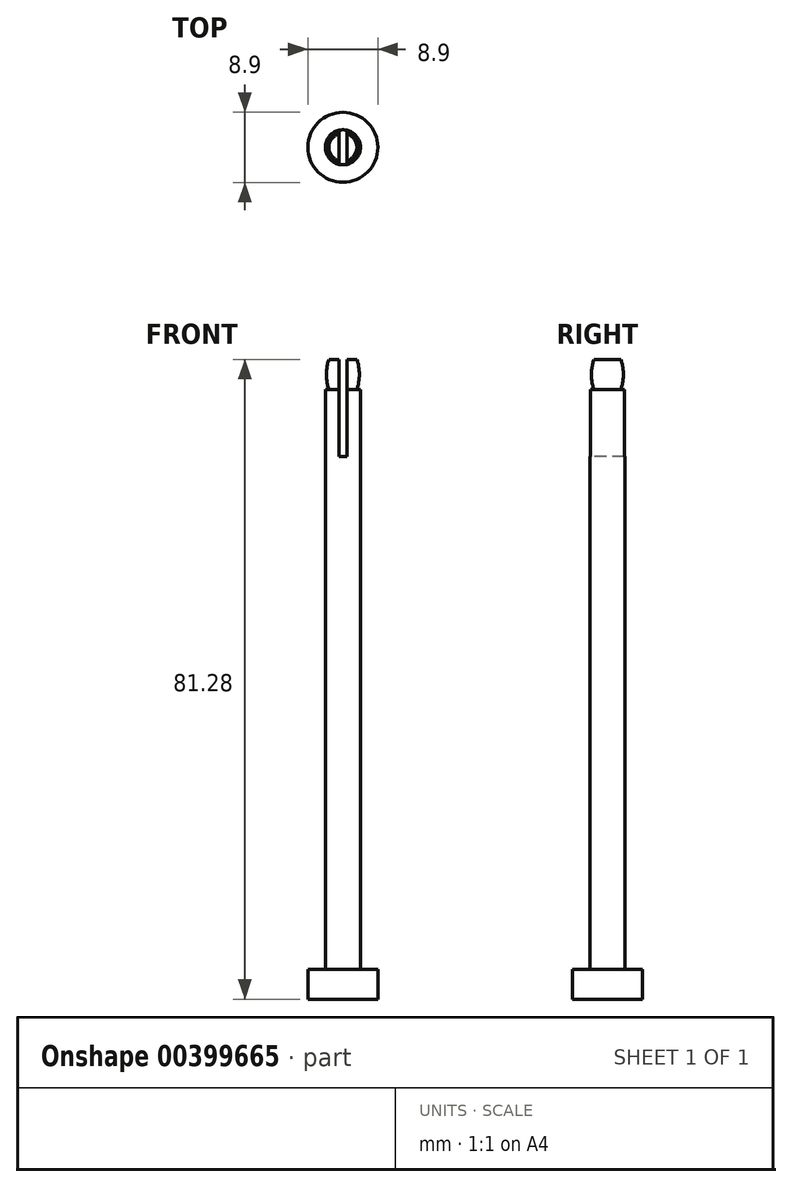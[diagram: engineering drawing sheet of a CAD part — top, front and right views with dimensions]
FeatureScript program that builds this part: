
annotation { "Feature Type Name" : "Feature", "Feature Type Description" : "" }
export const myFeature = defineFeature(function(context is Context, id is Id, definition is map)
    precondition{}
    {
        {
            var Q0;
            Q0=qCreatedBy(makeId("Top.planeOp"),FACE);
            var sketch = newSketch(context, id + "F0", { "sketchPlane" : qUnion([Q0])});
            skCircle(sketch, "E0", {"center": v(0, 0) * mm, "radius": 2.22 * mm});
            skSolve(sketch);
        }
        {
            var Q0;
            Q0=makeQuery(id+"F0.imprint","IMPRINT",FACE,{"disambiguationData":[TD([[makeQuery(id+"F0.imprint","IMPRINT",EDGE,{"derivedFrom":sQuery(id+"F0.wireOp",EDGE,"E0")}),1.0]])]});
            extrude(context, id + "F1", {"entities" : qUnion([Q0]), "depth" : 40.64 * mm, "hasSecondDirection" : true, "secondDirectionOppositeDirection" : true, "secondDirectionDepth" : 40.64 * mm});
        }
        {
            var Q0;
            Q0=makeQuery(id+"F1.opExtrude","CAP_FACE",FACE,{"disambiguationData":[OSD([sQuery(id+"F0.wireOp",EDGE,"E0")])],"isStart":true});
            var sketch = newSketch(context, id + "F2", { "sketchPlane" : qUnion([Q0])});
            skCircle(sketch, "E1", {"center": v(0, 0) * mm, "radius": 4.45 * mm});
            skSolve(sketch);
        }
        {
            var Q0;
            Q0=makeQuery(id+"F2.imprint","IMPRINT",FACE,{"disambiguationData":[TD([[makeQuery(id+"F2.imprint","IMPRINT",EDGE,{"derivedFrom":sQuery(id+"F2.wireOp",EDGE,"E1")}),1.0]])]});
            extrude(context, id + "F3", {"entities" : qUnion([Q0]), "operationType" : NewBodyOperationType.ADD, "oppositeDirection" : true, "depth" : 3.8 * mm});
        }
        {
            var Q0;
            Q0=qCreatedBy(makeId("Front.planeOp"),FACE);
            var sketch = newSketch(context, id + "F4", { "sketchPlane" : qUnion([Q0])});
            skLineSegment(sketch, "E2.bottom", {"start": v(0, 40.64) * mm, "end": v(-5.55, 40.64) * mm});
            skLineSegment(sketch, "E2.top", {"start": v(0, 36.83) * mm, "end": v(-5.55, 36.83) * mm});
            skLineSegment(sketch, "E2.left", {"start": v(0, 40.64) * mm, "end": v(0, 36.83) * mm});
            skLineSegment(sketch, "E2.right", {"start": v(-5.55, 40.64) * mm, "end": v(-5.55, 36.83) * mm});
            skArc(sketch, "E3", {"start": v(-1.78, 40.64) * mm, "mid": v(-2.1, 38.74) * mm, "end": v(-1.78, 36.83) * mm});
            skSolve(sketch);
        }
        {
            var Q0;
            {var subQ0=sQuery(id+"F4.wireOp",EDGE,"E2.right");Q0=makeQuery(id+"F4.imprint","IMPRINT",FACE,{"disambiguationData":[TD([[makeQuery(id+"F4.imprint","IMPRINT",EDGE,{"derivedFrom":subQ0}),1.0]])]});}
            var Q1;
            Q1=sQuery(id+"F4.wireOp",EDGE,"E2.left");
            revolve(context, id + "F5", {"operationType" : NewBodyOperationType.REMOVE, "entities" : qUnion([Q0]), "axis" : qUnion([Q1]), "revolveType" : RevolveType.FULL, "oppositeDirection" : true});
        }
        {
            var Q0;
            Q0=qCreatedBy(makeId("Front.planeOp"),FACE);
            var sketch = newSketch(context, id + "F6", { "sketchPlane" : qUnion([Q0])});
            skLineSegment(sketch, "E4.bottom", {"start": v(-0.5, 41.04) * mm, "end": v(0.5, 41.04) * mm});
            skLineSegment(sketch, "E4.top", {"start": v(-0.5, 28.34) * mm, "end": v(0.5, 28.34) * mm});
            skLineSegment(sketch, "E4.left", {"start": v(-0.5, 41.04) * mm, "end": v(-0.5, 28.34) * mm});
            skLineSegment(sketch, "E4.right", {"start": v(0.5, 41.04) * mm, "end": v(0.5, 28.34) * mm});
            skPoint(sketch, "E4.middle", {"position": v(0, 34.69) * mm});
            skSolve(sketch);
        }
        {
            var Q0;
            Q0=makeQuery(id+"F6.imprint","IMPRINT",FACE,{"disambiguationData":[TD([[makeQuery(id+"F6.imprint","IMPRINT",EDGE,{"derivedFrom":sQuery(id+"F6.wireOp",EDGE,"E4.bottom")}),-1.0]])]});
            extrude(context, id + "F7", {"entities" : qUnion([Q0]), "operationType" : NewBodyOperationType.REMOVE, "oppositeDirection" : true, "depth" : 25.4 * mm, "hasSecondDirection" : true, "secondDirectionOppositeDirection" : false, "secondDirectionDepth" : 25.4 * mm});
        }
    });
